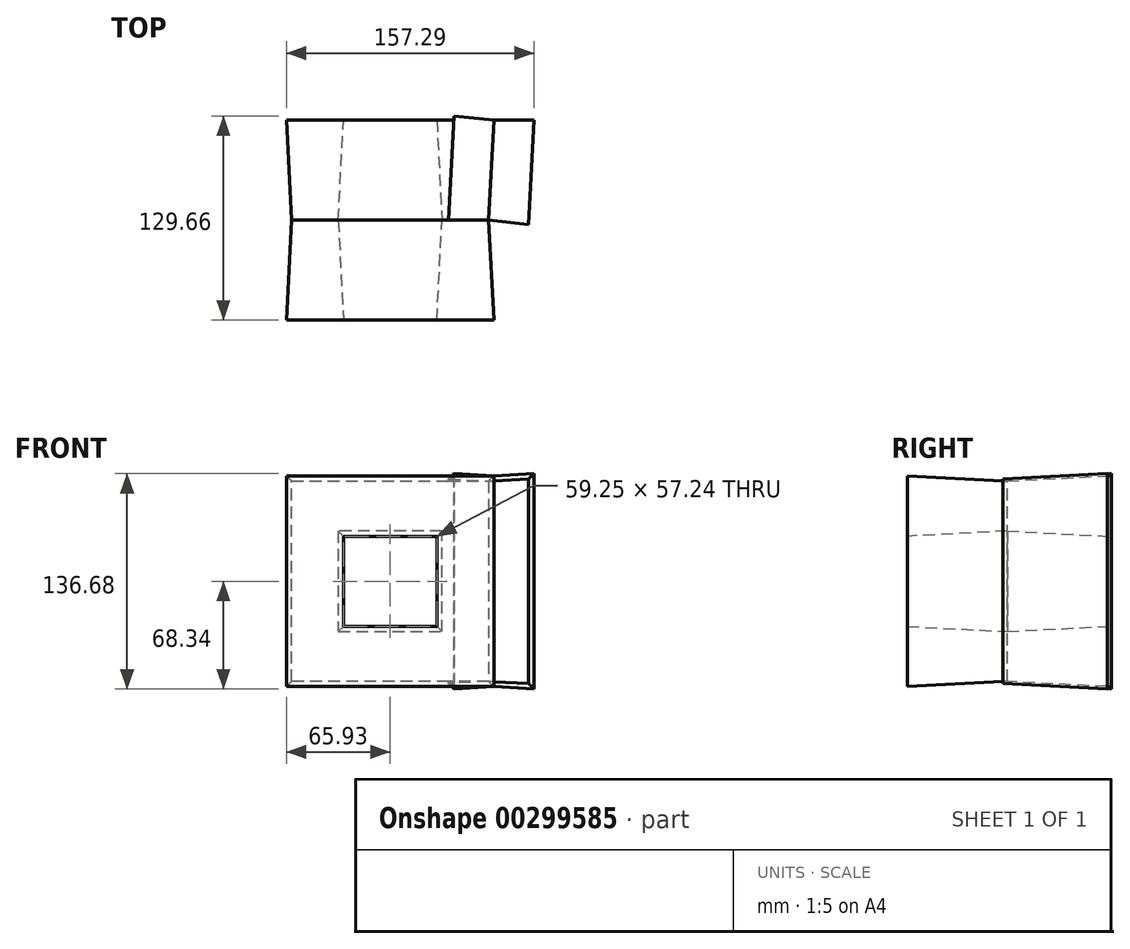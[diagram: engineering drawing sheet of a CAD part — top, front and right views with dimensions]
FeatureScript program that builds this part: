
annotation { "Feature Type Name" : "Feature", "Feature Type Description" : "" }
export const myFeature = defineFeature(function(context is Context, id is Id, definition is map)
    precondition{}
    {
        {
            var Q0;
            Q0=qCreatedBy(makeId("Front.planeOp"),FACE);
            var sketch = newSketch(context, id + "F0", { "sketchPlane" : qUnion([Q0])});
            skLineSegment(sketch, "E0.bottom", {"start": v(-62.6, 63.6) * mm, "end": v(62.6, 63.6) * mm});
            skLineSegment(sketch, "E0.top", {"start": v(-62.6, -63.6) * mm, "end": v(62.6, -63.6) * mm});
            skLineSegment(sketch, "E0.left", {"start": v(-62.6, 63.6) * mm, "end": v(-62.6, -63.6) * mm});
            skLineSegment(sketch, "E0.right", {"start": v(62.6, 63.6) * mm, "end": v(62.6, -63.6) * mm});
            skPoint(sketch, "E0.middle", {"position": v(0, 0) * mm});
            skCircle(sketch, "E1", {"center": v(0, 0) * mm, "radius": 28.97 * mm});
            skLineSegment(sketch, "E2.bottom", {"start": v(-32.95, 31.95) * mm, "end": v(32.95, 31.95) * mm});
            skLineSegment(sketch, "E2.top", {"start": v(-32.95, -31.95) * mm, "end": v(32.95, -31.95) * mm});
            skLineSegment(sketch, "E2.left", {"start": v(-32.95, 31.95) * mm, "end": v(-32.95, -31.95) * mm});
            skLineSegment(sketch, "E2.right", {"start": v(32.95, 31.95) * mm, "end": v(32.95, -31.95) * mm});
            skCircle(sketch, "E3", {"center": v(-147.22, 9.56) * mm, "radius": 15.61 * mm});
            skPoint(sketch, "E3.first.point", {"position": v(-162.47, 12.95) * mm});
            skPoint(sketch, "E3.second.point", {"position": v(-131.67, 10.94) * mm});
            skPoint(sketch, "E3.third.point", {"position": v(-147.79, -6.04) * mm});
            skSolve(sketch);
        }
        {
            var Q0;
            Q0=makeQuery(id+"F0.imprint","IMPRINT",FACE,{"disambiguationData":[TD([[makeQuery(id+"F0.imprint","IMPRINT",EDGE,{"derivedFrom":sQuery(id+"F0.wireOp",EDGE,"E0.bottom")}),-1.0]])]});
            extrude(context, id + "F1", {"entities" : qUnion([Q0]), "endBound" : BoundingType.SYMMETRIC, "depth" : 127 * mm, "hasDraft" : true, "draftAngle" : 3 * degree});
        }
        {
            var Q0;
            Q0=makeQuery(id+"F1.*.split.splitOp","SPLIT",FACE,{"derivedFrom":makeQuery(id+"F1.opExtrude","SWEPT_FACE",FACE,{"disambiguationData":[OSD([sQuery(id+"F0.wireOp",EDGE,"E0.right")])]}),"isFromBackBody":true});
            extrude(context, id + "F2", {"entities" : qUnion([Q0]), "operationType" : NewBodyOperationType.ADD, "endBound" : BoundingType.SYMMETRIC, "depth" : 50.8 * mm, "hasDraft" : true, "draftAngle" : 3 * degree});
        }
    });
